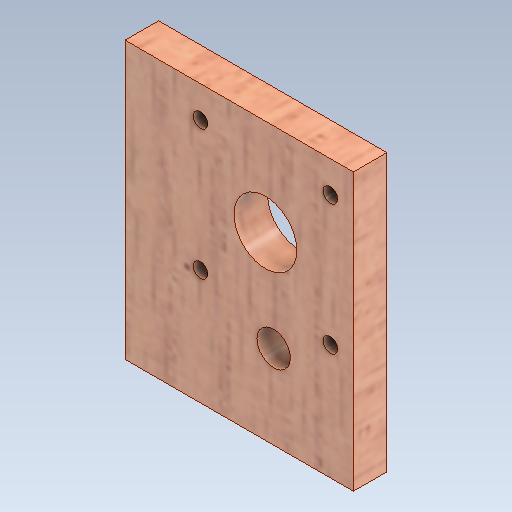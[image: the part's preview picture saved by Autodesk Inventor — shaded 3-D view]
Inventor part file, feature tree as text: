
AUTODESK INVENTOR PART (.ipt)
format: ipt  version: 2020 (Build 240168000, 168)  size: 270,848 bytes
history: native  units: mm
features: extrude x3, sketch x3
ambient origin geometry x8: Origin, YZ Plane, XZ Plane, XY Plane, X Axis, Y Axis, Z Axis, Center Point
bodies: Solid1 (feature_tree)
feature tree (6):
  extrude  "Extrusion1"  Depth=66.0mm
  extrude  "Extrusion2"  TaperAngle=0.0deg  [1 undecoded]
  extrude  "Extrusion4"  Depth=8.0mm
  sketch  "Sketch1"  dims[d0=54.5mm d1=66.0mm]
  sketch  "Sketch2"  dims[d2=8.0mm d3=0.0mm d6=0.0mm d7=0.0mm]
  sketch  "Sketch4"  dims[d17=15.0mm d19=21.0mm d20=23.0mm d22=31.0mm d23=3.5mm d24=8.0mm d25=20.0mm d26=19.030905mm d27=0.0mm d28=0.0mm]
note: 1 required parameter value undecoded (feature->parameter linkage not recoverable at this tier; creation-order binding heuristic only, values carry confidence <= 0.55)
